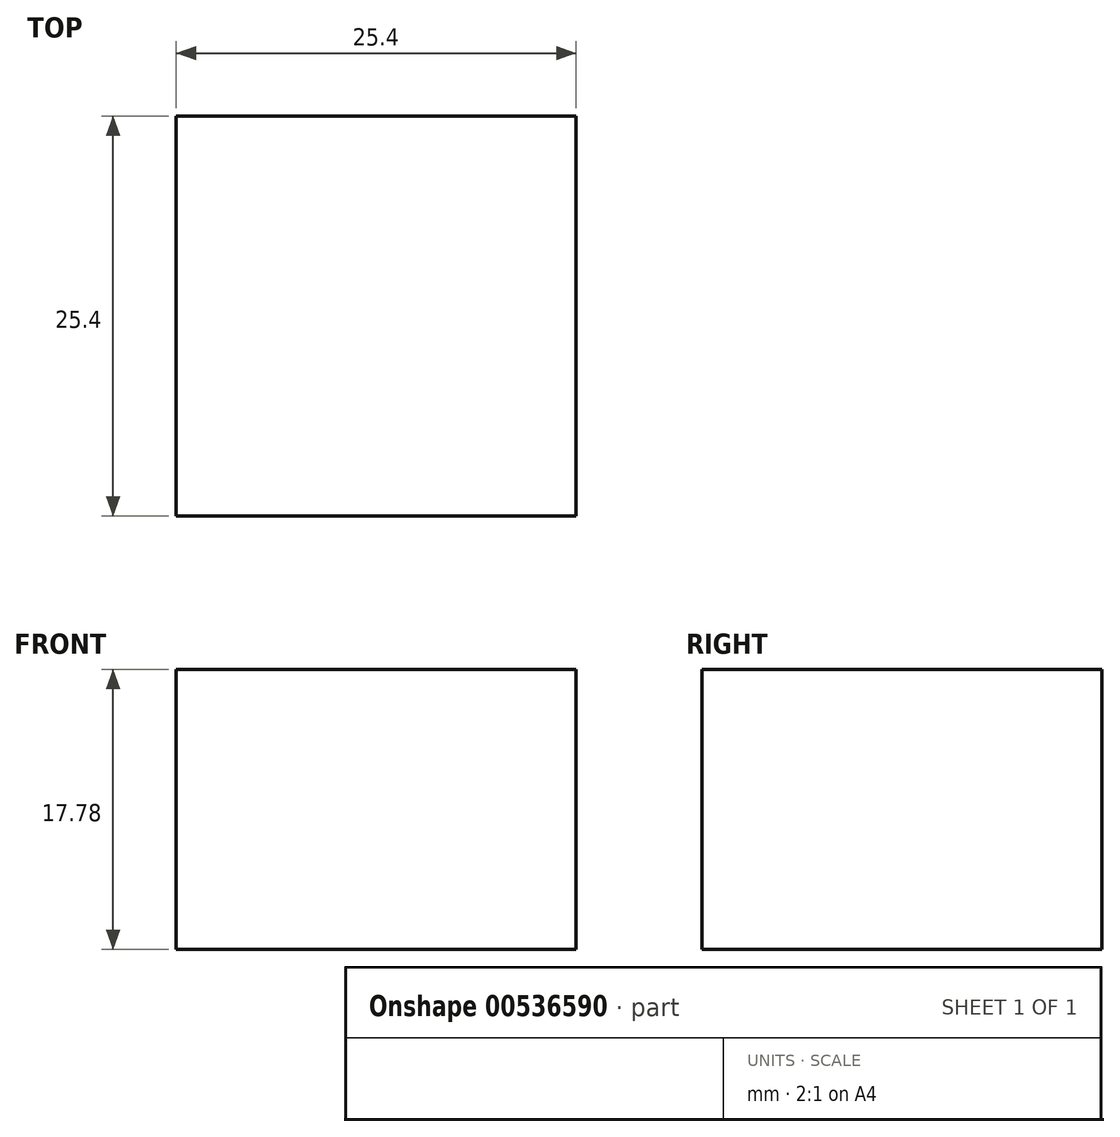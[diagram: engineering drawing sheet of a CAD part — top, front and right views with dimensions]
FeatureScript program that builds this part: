
annotation { "Feature Type Name" : "Feature", "Feature Type Description" : "" }
export const myFeature = defineFeature(function(context is Context, id is Id, definition is map)
    precondition{}
    {
        {
            var Q0;
            Q0=qCreatedBy(makeId("Top.planeOp"),FACE);
            var sketch = newSketch(context, id + "F0", { "sketchPlane" : qUnion([Q0])});
            skLineSegment(sketch, "E0.bottom", {"start": v(-16.31, 23.52) * mm, "end": v(9.09, 23.52) * mm});
            skLineSegment(sketch, "E0.top", {"start": v(-16.31, -1.88) * mm, "end": v(9.09, -1.88) * mm});
            skLineSegment(sketch, "E0.left", {"start": v(-16.31, 23.52) * mm, "end": v(-16.31, -1.88) * mm});
            skLineSegment(sketch, "E0.right", {"start": v(9.09, 23.52) * mm, "end": v(9.09, -1.88) * mm});
            skSolve(sketch);
        }
        {
            var Q0;
            Q0 = qSketchRegion(id + "F0", true);
            extrude(context, id + "F1", {"entities" : qUnion([Q0]), "depth" : 17.78 * mm, "offsetDistance" : 25.4 * mm});
        }
    });
